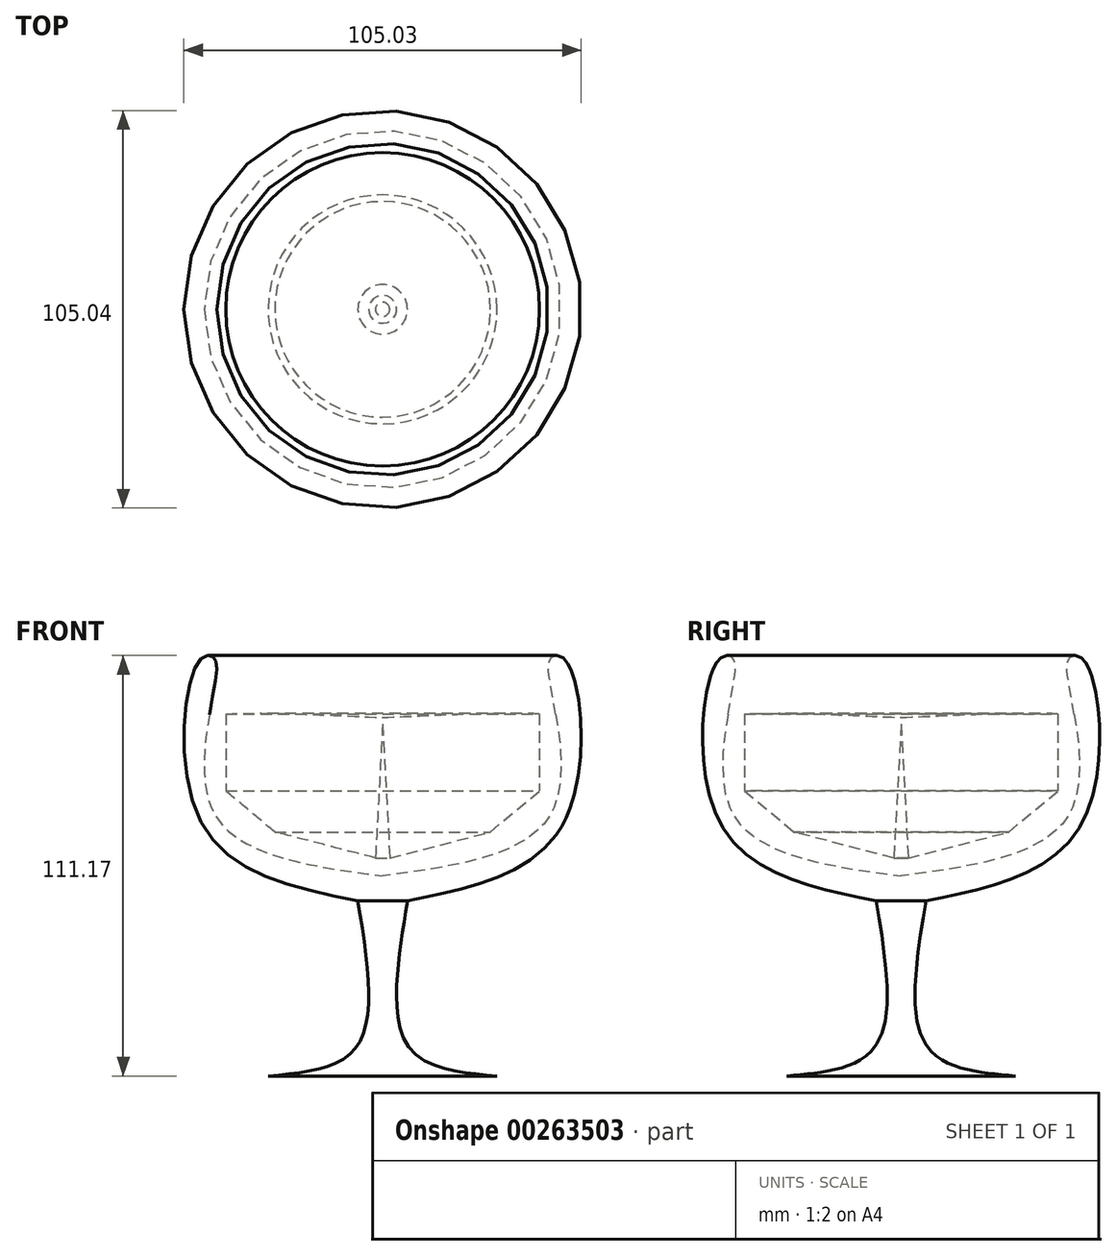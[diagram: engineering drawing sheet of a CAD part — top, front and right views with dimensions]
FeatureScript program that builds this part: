
annotation { "Feature Type Name" : "Feature", "Feature Type Description" : "" }
export const myFeature = defineFeature(function(context is Context, id is Id, definition is map)
    precondition{}
    {
        {
            var Q0;
            Q0=qCreatedBy(makeId("Front.planeOp"),FACE);
            var sketch = newSketch(context, id + "F0", { "sketchPlane" : qUnion([Q0])});
            skLineSegment(sketch, "E0", {"start": v(0, 0) * mm, "end": v(-30.26, 0) * mm});
            skFitSpline(sketch, "E1", {"points": [v(-30.26, 0) * mm, v(-6.93, 7.66) * mm, v(-6.56, 46.3) * mm], "startDerivative": vector(64.12, 5.69) * mm, "endDerivative": vector(-13.8, 83.96) * mm});
            skFitSpline(sketch, "E2", {"points": [v(-6.56, 46.3) * mm, v(-48.12, 67.44) * mm, v(-48.48, 109.72) * mm, v(-44.84, 110.82) * mm, v(-44.1, 104.98) * mm, v(-44.84, 69.99) * mm, v(0, 52.86) * mm], "startDerivative": vector(-230.55, 46.59) * mm, "endDerivative": vector(256.98, -34.85) * mm});
            skLineSegment(sketch, "E3", {"start": v(0, 52.86) * mm, "end": v(0, 0) * mm});
            skFitSpline(sketch, "E4", {"points": [v(-45.77, 95.6) * mm, v(-32.44, 95.87) * mm, v(-16.4, 95.5) * mm, v(0, 94.78) * mm], "startDerivative": vector(41.64, 1.3) * mm, "endDerivative": vector(47.22, -2.25) * mm});
            skLineSegment(sketch, "E5", {"start": v(0, 52.86) * mm, "end": v(0, 94.78) * mm});
            skLineSegment(sketch, "E6", {"start": v(-41.45, 95.74) * mm, "end": v(-41.45, 75.33) * mm});
            skLineSegment(sketch, "E7", {"start": v(-41.45, 75.33) * mm, "end": v(-28.49, 64.51) * mm});
            skLineSegment(sketch, "E8", {"start": v(-28.49, 64.51) * mm, "end": v(-1.88, 57.65) * mm});
            skLineSegment(sketch, "E9", {"start": v(-1.88, 57.65) * mm, "end": v(0, 93.01) * mm});
            skSolve(sketch);
        }
        {
            var Q0;
            Q0=makeQuery(id+"F0.imprint","IMPRINT",FACE,{"disambiguationData":[TD([[makeQuery(id+"F0.imprint","IMPRINT",EDGE,{"derivedFrom":sQuery(id+"F0.wireOp",EDGE,"E0")}),-1.0]])]});
            var Q1;
            {var subQ2=sQuery(id+"F0.wireOp",EDGE,"E4");Q1=makeQuery(id+"F0.imprint","IMPRINT",FACE,{"disambiguationData":[TD([[makeQuery(id+"F0.imprint","IMPRINT",EDGE,{"derivedFrom":subQ2}),-1.0]])]});}
            var Q2;
            Q2=sQuery(id+"F0.wireOp",EDGE,"E5");
            revolve(context, id + "F1", {"entities" : qUnion([Q0, Q1]), "axis" : qUnion([Q2]), "revolveType" : RevolveType.FULL});
        }
    });
